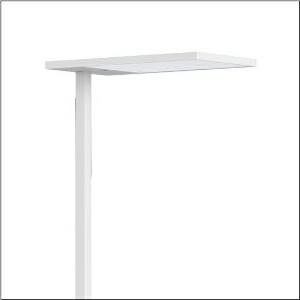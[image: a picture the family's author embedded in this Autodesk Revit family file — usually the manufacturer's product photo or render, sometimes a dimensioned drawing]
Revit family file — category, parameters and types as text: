
# Revit family: silica_r__21_floor_r_51mx53sg4dw_45fa
name_source: partatom
category: Lighting Fixtures
units: mm (PartAtom-declared; Revit-internal decimal feet)

## family parameters
Cut with Voids When Loaded = No
Host = Face
Light Source = No
Part Type = Normal
Room Calculation Point = No
Round Connector Dimension = Use Diameter
Shared = No

## types (1)
- Silica® 21 Floor R (1 x LED, 15000 lm, 106.4 W, 4000K)
    Apparent Load = 106 VA
    CIE Flux Codes = 54 86 97 13 100
    Color Rendering = 80
    Color Temperature = 4000K
    Default Elevation = 1800 mm
    Description = Silica® 21 Floor R, floorstanding luminaire, of PMMA, primary optical cover: prismatic diffuser, of PMMA, CAT 2 (L<= 3000cd/m²), light emission: indirect/direct distribution, primary light characteristic: symmetric, installation type: not mounted, LED, rated luminous flux: 15.000lm, luminous efficacy: 141lm/W, light colour: 840, colour temperature: 4000K, control gear: ECG DALI, daylight-dependent control, mains connection: 230V, 50Hz, connection cable pre-assembled, cable length: 2,5m, rated input power: 106.4W, luminaire head, of aluminium, traffic white (RAL 9016), length: 650mm, width: 350mm, supporting column, angular, of aluminium, traffic white (RAL 9016), baseplate, of steel, traffic white (RAL 9016), protection rating (complete): IP20, insulation class (complete): insulation class I (protective earthing), certification: CE, standard: EN 50419, packaging unit: 1 piece
    Height = 18 mm
    Lamp = 1 x LED
    Lamp Light Flux = 15000 lm
    Lamp Power = 106.4 W
    Lamp count = 1
    Length = 650 mm
    Luminous efficacy = 141 lm/W
    Manufacturer = Siteco
    ModVariant = No
    Model = 51MX53SG4DW
    Mounting Place = Floor
    Mounting Type = Freestanding
    Number of Poles = 1
    OnlyDefault = Yes
    Power Factor = 1
    Product Name = Silica® 21 Floor R
    Product group = floorstanding luminaire
    ProductGroupID = 1302
    Protection Class = Protection class I
    Protection Degree = IP 20
    RLX_Detail_Level = 1
    RlxData = <blob elided: 18665 chars, md5=64557df8>
    Socket = socket
    Standby Power = 0 W
    System Light Flux = 15000 lm
    System Power = 106 W
    Type Comments = Product without accessories
    Type Image = l_1003935.jpg
    URL = http://relux.com
    VarID = ---
    Voltage = 0 V
    Weight = 0.00 kg
    Width = 350 mm

## geometry (parser evidence)
native form markers: Blend x4, Sweep x15
no freeform markers — native parametric forms only
